# Revit family: Gira_216300
name_source: partatom
category: Electrical Fixtures
revit_build: Autodesk Revit 2017 (Build: 20160225_1515(x64)
units: mm (PartAtom-declared; Revit-internal decimal feet)

## family parameters
Cut with Voids When Loaded = No
Host = Face
Maintain Annotation Orientation = No
Part Type = Normal
Room Calculation Point = No
Round Connector Dimension = Use Diameter
Shared = No

## types (1)
- Fan coil act. KNX DRA
    BIM = https://media.live.bim.site 8f.rfa
    BIMSITE_PRODUCT_ID = e50a8b9e110624fc39c6d2d0b3aa76b6184317be
    Bus connection included = No
    Cost = 0 $
    Default Elevation = 1219 mm
    Description = Fan coil act.DRA KNX KNX fan coil actuator,DRA plus Features: - Fan coil actuator for operation of ventilator convectors (fan coil units), implemented for room air conditioning. - The actuator receives telegrams, for example from room temperature controllers, and converts corrected variable telegrams into equivalent fan speeds and valve positions. - Connection of a ventilator convector with up to six ventilator gradations or connection of two ventilator convectors each with up to three fan speeds with double pipe systems. - Manual actuation. - Building site operation: Outputs can be operated manually without bus voltage with operating voltage only. - Operating modes for heating or cooling mode, or combined heating cooling mode. - Double tube or quadruple tube operation. Double tube system heats or cools via a shared water cycle. Quadruple tube system consists of separate flow and return for heating and cooling. - Individual or hierarchic switching of fan speeds. - Feedback, output indication, block function for each channel, level limitation. - Behaviour after bus voltage failure or bus mains voltage failure and following an ETS programming process can be configured. - Limit values can be set. - Cyclical or event-oriented transmission. - Free channels can be used for switching functions, e.g. for room lighting,Notes : - VDE approval in accordance with EN 60669-1, EN 60669-2-1. - Installation on DIN top-hat rail.
    GTIN = 4010337059387
    HAN = 216300
    Handschaltung = No
    HeinzeBIM = https://www.heinze.de
    LED controlling = No
    Local operation/hand operation = No
    Manufacturer = Gira
    Max. number of venetian-blind outputs = 0
    Max. switching current [Ampere] = 0
    Modulare Erweiterungsmöglichkeit = No
    Number of binary inputs = 0
    Number of inputs = 0
    Number of outputs = 0
    Rated current [Ampere] = 0
    Stellgröße schaltend = No
    Stellgröße stetig = No
    Suitable for C-load = No
    URL = https://www.gira.de
    Ventilschutzfunktion = No
    Verschiedene Phasen anschließbar = No
    With switch function = No

## geometry (parser evidence)
native form markers: Blend x2, Sweep x3
no freeform markers — native parametric forms only
